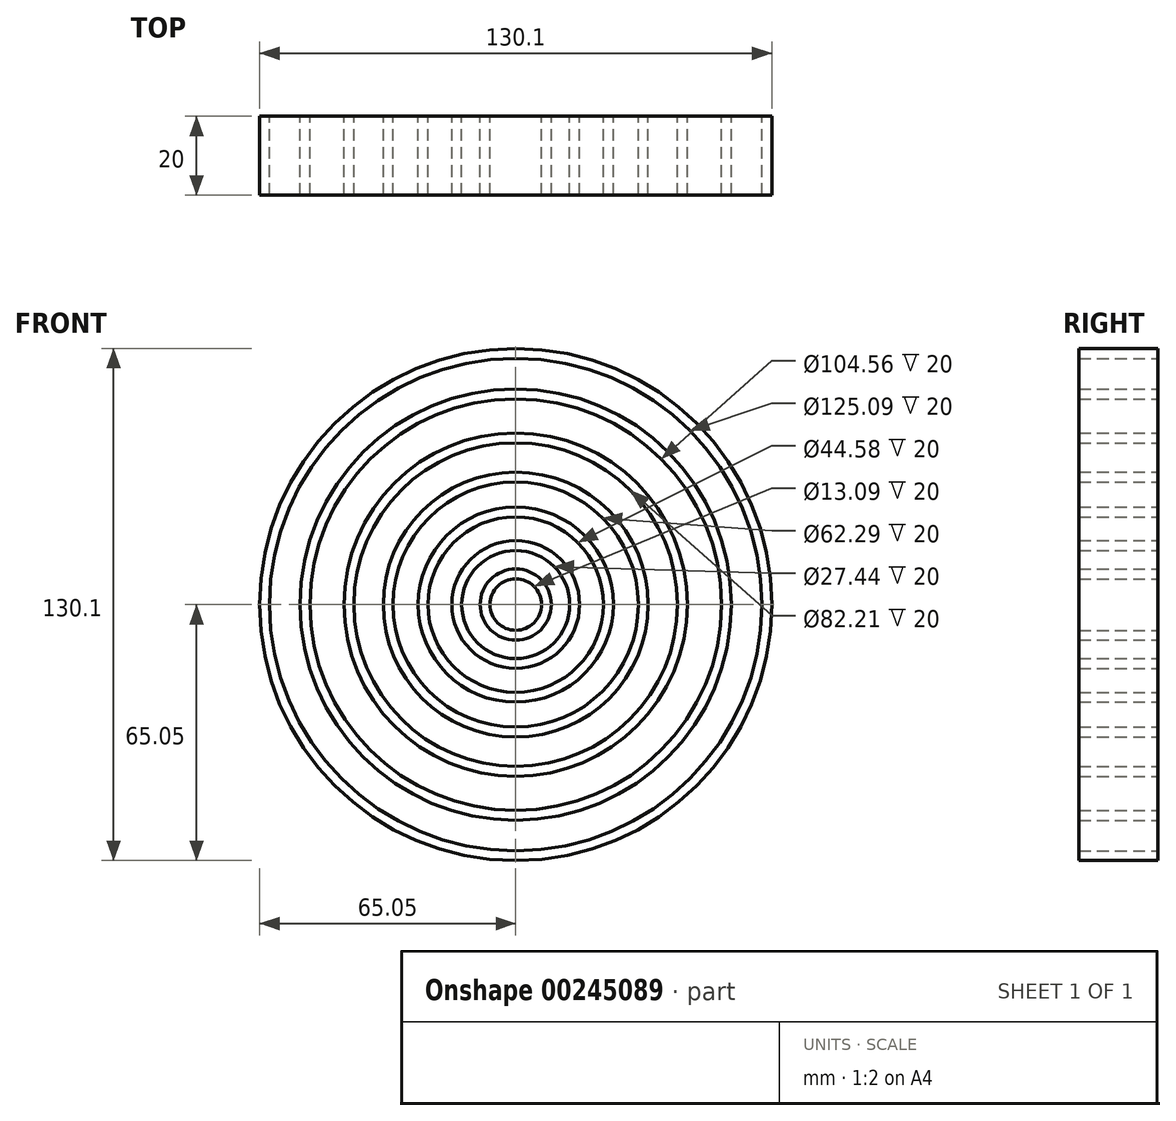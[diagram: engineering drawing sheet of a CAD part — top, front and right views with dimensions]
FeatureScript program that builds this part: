
annotation { "Feature Type Name" : "Feature", "Feature Type Description" : "" }
export const myFeature = defineFeature(function(context is Context, id is Id, definition is map)
    precondition{}
    {
        {
            var Q0;
            Q0=qCreatedBy(makeId("Front.planeOp"),FACE);
            var sketch = newSketch(context, id + "F0", { "sketchPlane" : qUnion([Q0])});
            skCircle(sketch, "E0", {"center": v(0, 0) * mm, "radius": 65.05 * mm});
            skSolve(sketch);
        }
        {
            var Q0;
            Q0=makeQuery(id+"F0.imprint","IMPRINT",FACE,{"disambiguationData":[TD([[makeQuery(id+"F0.imprint","IMPRINT",EDGE,{"derivedFrom":sQuery(id+"F0.wireOp",EDGE,"E0")}),1.0]])]});
            extrude(context, id + "F1", {"entities" : qUnion([Q0]), "endBound" : BoundingType.SYMMETRIC, "depth" : 20 * mm});
        }
        {
            var Q0;
            Q0=makeQuery(id+"F1.opExtrude","CAP_FACE",FACE,{"disambiguationData":[OSD([sQuery(id+"F0.wireOp",EDGE,"E0")])],"isStart":false});
            var Q1;
            Q1=makeQuery(id+"F1.opExtrude","CAP_FACE",FACE,{"disambiguationData":[OSD([sQuery(id+"F0.wireOp",EDGE,"E0")])],"isStart":true});
            shell(context, id + "F2", {"entities" : qUnion([Q0, Q1]), "thickness" : 2.5 * mm});
        }
        {
            var Q0;
            Q0=qCreatedBy(makeId("Front.planeOp"),FACE);
            var sketch = newSketch(context, id + "F3", { "sketchPlane" : qUnion([Q0])});
            skCircle(sketch, "E1", {"center": v(0, 0) * mm, "radius": 54.78 * mm});
            skSolve(sketch);
        }
        {
            var Q0;
            Q0=makeQuery(id+"F3.imprint","IMPRINT",FACE,{"disambiguationData":[TD([[makeQuery(id+"F3.imprint","IMPRINT",EDGE,{"derivedFrom":sQuery(id+"F3.wireOp",EDGE,"E1")}),1.0]])]});
            extrude(context, id + "F4", {"entities" : qUnion([Q0]), "endBound" : BoundingType.SYMMETRIC, "depth" : 20 * mm});
        }
        {
            var Q0;
            Q0=makeQuery(id+"F4.opExtrude","CAP_FACE",FACE,{"disambiguationData":[OSD([sQuery(id+"F3.wireOp",EDGE,"E1")])],"isStart":false});
            var Q1;
            Q1=makeQuery(id+"F4.opExtrude","CAP_FACE",FACE,{"disambiguationData":[OSD([sQuery(id+"F3.wireOp",EDGE,"E1")])],"isStart":true});
            shell(context, id + "F5", {"entities" : qUnion([Q0, Q1]), "thickness" : 2.5 * mm});
        }
        {
            var Q0;
            Q0=qCreatedBy(makeId("Front.planeOp"),FACE);
            var sketch = newSketch(context, id + "F6", { "sketchPlane" : qUnion([Q0])});
            skCircle(sketch, "E2", {"center": v(0, 0) * mm, "radius": 43.6 * mm});
            skSolve(sketch);
        }
        {
            var Q0;
            Q0=makeQuery(id+"F6.imprint","IMPRINT",FACE,{"disambiguationData":[TD([[makeQuery(id+"F6.imprint","IMPRINT",EDGE,{"derivedFrom":sQuery(id+"F6.wireOp",EDGE,"E2")}),1.0]])]});
            extrude(context, id + "F7", {"entities" : qUnion([Q0]), "endBound" : BoundingType.SYMMETRIC, "depth" : 20 * mm});
        }
        {
            var Q0;
            Q0=makeQuery(id+"F7.opExtrude","CAP_FACE",FACE,{"disambiguationData":[OSD([sQuery(id+"F6.wireOp",EDGE,"E2")])],"isStart":false});
            var Q1;
            Q1=makeQuery(id+"F7.opExtrude","CAP_FACE",FACE,{"disambiguationData":[OSD([sQuery(id+"F6.wireOp",EDGE,"E2")])],"isStart":true});
            shell(context, id + "F8", {"entities" : qUnion([Q0, Q1]), "thickness" : 2.5 * mm});
        }
        {
            var Q0;
            Q0=qCreatedBy(makeId("Front.planeOp"),FACE);
            var sketch = newSketch(context, id + "F9", { "sketchPlane" : qUnion([Q0])});
            skCircle(sketch, "E3", {"center": v(0, 0) * mm, "radius": 33.64 * mm});
            skSolve(sketch);
        }
        {
            var Q0;
            Q0=makeQuery(id+"F9.imprint","IMPRINT",FACE,{"disambiguationData":[TD([[makeQuery(id+"F9.imprint","IMPRINT",EDGE,{"derivedFrom":sQuery(id+"F9.wireOp",EDGE,"E3")}),1.0]])]});
            extrude(context, id + "F10", {"entities" : qUnion([Q0]), "endBound" : BoundingType.SYMMETRIC, "depth" : 20 * mm});
        }
        {
            var Q0;
            Q0=makeQuery(id+"F10.opExtrude","CAP_FACE",FACE,{"disambiguationData":[OSD([sQuery(id+"F9.wireOp",EDGE,"E3")])],"isStart":false});
            var Q1;
            Q1=makeQuery(id+"F10.opExtrude","CAP_FACE",FACE,{"disambiguationData":[OSD([sQuery(id+"F9.wireOp",EDGE,"E3")])],"isStart":true});
            shell(context, id + "F11", {"entities" : qUnion([Q0, Q1]), "thickness" : 2.5 * mm});
        }
        {
            var Q0;
            Q0=qCreatedBy(makeId("Front.planeOp"),FACE);
            var sketch = newSketch(context, id + "F12", { "sketchPlane" : qUnion([Q0])});
            skCircle(sketch, "E4", {"center": v(0, 0) * mm, "radius": 24.8 * mm});
            skSolve(sketch);
        }
        {
            var Q0;
            Q0=makeQuery(id+"F12.imprint","IMPRINT",FACE,{"disambiguationData":[TD([[makeQuery(id+"F12.imprint","IMPRINT",EDGE,{"derivedFrom":sQuery(id+"F12.wireOp",EDGE,"E4")}),1.0]])]});
            extrude(context, id + "F13", {"entities" : qUnion([Q0]), "endBound" : BoundingType.SYMMETRIC, "depth" : 20 * mm});
        }
        {
            var Q0;
            Q0=makeQuery(id+"F13.opExtrude","CAP_FACE",FACE,{"disambiguationData":[OSD([sQuery(id+"F12.wireOp",EDGE,"E4")])],"isStart":false});
            var Q1;
            Q1=makeQuery(id+"F13.opExtrude","CAP_FACE",FACE,{"disambiguationData":[OSD([sQuery(id+"F12.wireOp",EDGE,"E4")])],"isStart":true});
            shell(context, id + "F14", {"entities" : qUnion([Q0, Q1]), "thickness" : 2.5 * mm});
        }
        {
            var Q0;
            Q0=qCreatedBy(makeId("Front.planeOp"),FACE);
            var sketch = newSketch(context, id + "F15", { "sketchPlane" : qUnion([Q0])});
            skCircle(sketch, "E5", {"center": v(0, 0) * mm, "radius": 16.22 * mm});
            skSolve(sketch);
        }
        {
            var Q0;
            Q0=makeQuery(id+"F15.imprint","IMPRINT",FACE,{"disambiguationData":[TD([[makeQuery(id+"F15.imprint","IMPRINT",EDGE,{"derivedFrom":sQuery(id+"F15.wireOp",EDGE,"E5")}),1.0]])]});
            extrude(context, id + "F16", {"entities" : qUnion([Q0]), "endBound" : BoundingType.SYMMETRIC, "depth" : 20 * mm});
        }
        {
            var Q0;
            Q0=makeQuery(id+"F16.opExtrude","CAP_FACE",FACE,{"disambiguationData":[OSD([sQuery(id+"F15.wireOp",EDGE,"E5")])],"isStart":false});
            var Q1;
            Q1=makeQuery(id+"F16.opExtrude","CAP_FACE",FACE,{"disambiguationData":[OSD([sQuery(id+"F15.wireOp",EDGE,"E5")])],"isStart":true});
            shell(context, id + "F17", {"entities" : qUnion([Q0, Q1]), "thickness" : 2.5 * mm});
        }
        {
            var Q0;
            Q0=qCreatedBy(makeId("Front.planeOp"),FACE);
            var sketch = newSketch(context, id + "F18", { "sketchPlane" : qUnion([Q0])});
            skCircle(sketch, "E6", {"center": v(0, 0) * mm, "radius": 9.04 * mm});
            skSolve(sketch);
        }
        {
            var Q0;
            Q0=makeQuery(id+"F18.imprint","IMPRINT",FACE,{"disambiguationData":[TD([[makeQuery(id+"F18.imprint","IMPRINT",EDGE,{"derivedFrom":sQuery(id+"F18.wireOp",EDGE,"E6")}),1.0]])]});
            extrude(context, id + "F19", {"entities" : qUnion([Q0]), "endBound" : BoundingType.SYMMETRIC, "depth" : 20 * mm});
        }
        {
            var Q0;
            Q0=makeQuery(id+"F19.opExtrude","CAP_FACE",FACE,{"disambiguationData":[OSD([sQuery(id+"F18.wireOp",EDGE,"E6")])],"isStart":false});
            var Q1;
            Q1=makeQuery(id+"F19.opExtrude","CAP_FACE",FACE,{"disambiguationData":[OSD([sQuery(id+"F18.wireOp",EDGE,"E6")])],"isStart":true});
            shell(context, id + "F20", {"entities" : qUnion([Q0, Q1]), "thickness" : 2.5 * mm});
        }
    });
